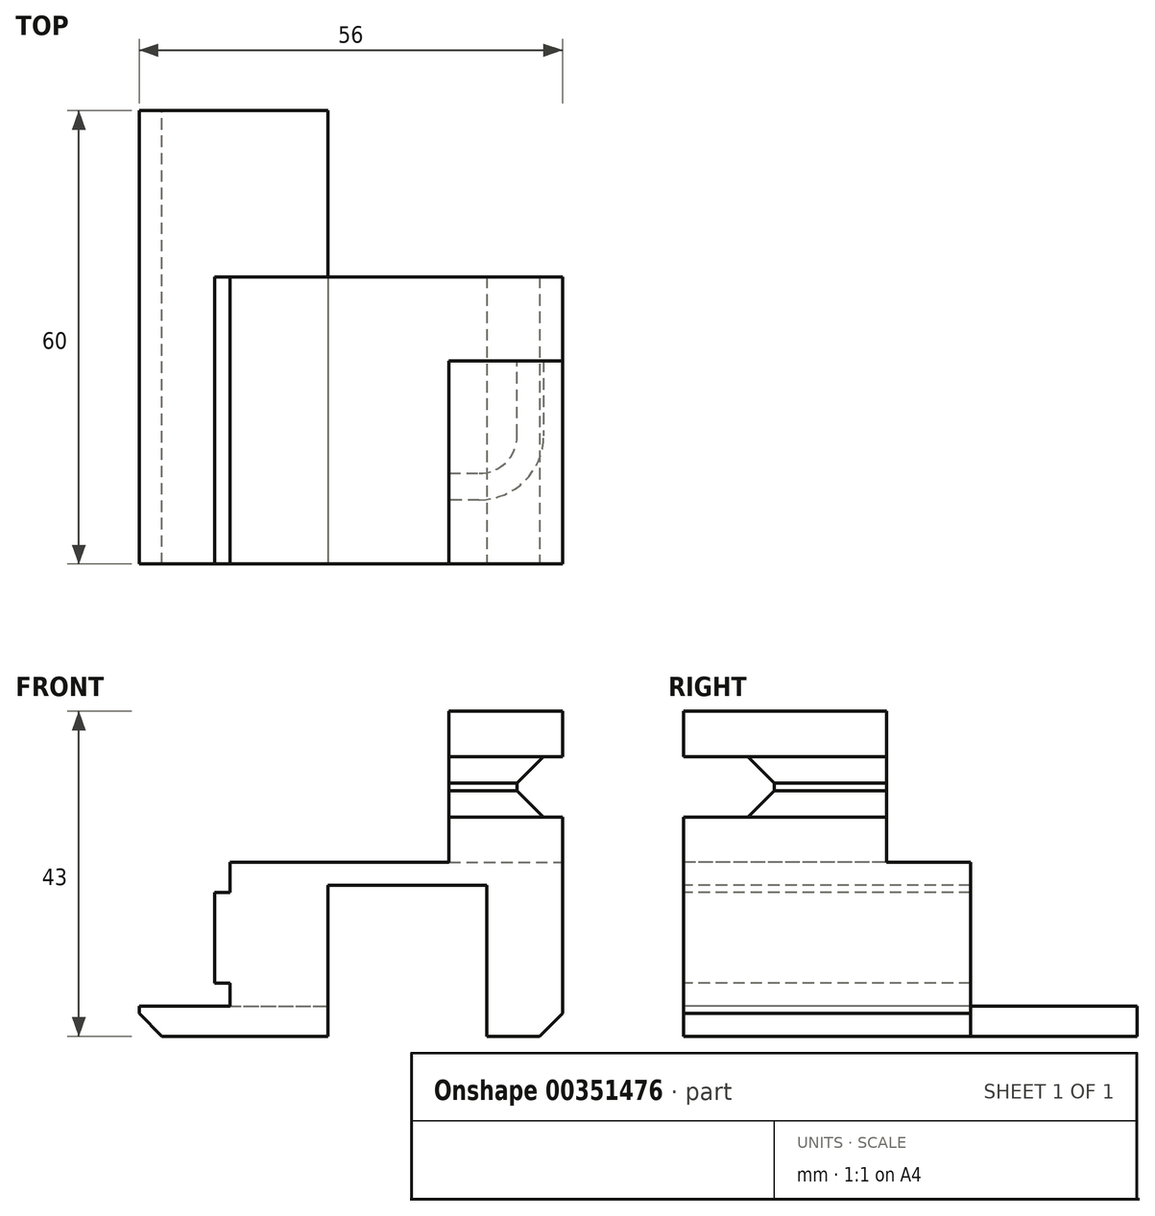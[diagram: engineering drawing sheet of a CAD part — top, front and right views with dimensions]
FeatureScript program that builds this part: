
annotation { "Feature Type Name" : "Feature", "Feature Type Description" : "" }
export const myFeature = defineFeature(function(context is Context, id is Id, definition is map)
    precondition{}
    {
        {
            var Q0;
            Q0=qCreatedBy(makeId("Front.planeOp"),FACE);
            var sketch = newSketch(context, id + "F0", { "sketchPlane" : qUnion([Q0])});
            skLineSegment(sketch, "E0", {"start": v(0, 0) * mm, "end": v(25, 0) * mm});
            skLineSegment(sketch, "E1", {"start": v(25, 0) * mm, "end": v(25, 20) * mm});
            skLineSegment(sketch, "E2", {"start": v(25, 20) * mm, "end": v(46, 20) * mm});
            skLineSegment(sketch, "E3", {"start": v(46, 20) * mm, "end": v(46, 0) * mm});
            skLineSegment(sketch, "E4", {"start": v(46, 0) * mm, "end": v(56, 0) * mm});
            skLineSegment(sketch, "E5", {"start": v(56, 0) * mm, "end": v(56, 43) * mm});
            skLineSegment(sketch, "E6", {"start": v(56, 43) * mm, "end": v(41, 43) * mm});
            skLineSegment(sketch, "E7", {"start": v(41, 43) * mm, "end": v(41, 23) * mm});
            skLineSegment(sketch, "E8", {"start": v(41, 23) * mm, "end": v(0, 23) * mm});
            skLineSegment(sketch, "E9", {"start": v(0, 23) * mm, "end": v(0, 0) * mm});
            skLineSegment(sketch, "E10", {"start": v(0, 4) * mm, "end": v(10, 4) * mm});
            skLineSegment(sketch, "E11", {"start": v(10, 4) * mm, "end": v(10, 23) * mm});
            skSolve(sketch);
        }
        {
            var Q0;
            {var subQ4=sQuery(id+"F0.wireOp",EDGE,"E0");Q0=makeQuery(id+"F0.imprint","IMPRINT",FACE,{"disambiguationData":[TD([[makeQuery(id+"F0.imprint","IMPRINT",EDGE,{"derivedFrom":subQ4}),1.0]])]});}
            extrude(context, id + "F1", {"entities" : qUnion([Q0]), "oppositeDirection" : true, "depth" : 60 * mm});
        }
        {
            var Q0;
            Q0=makeQuery(id+"F1.opExtrude","CAP_FACE",FACE,{"disambiguationData":[OSD([sQuery(id+"F0.wireOp",EDGE,"E0"),sQuery(id+"F0.wireOp",EDGE,"E1"),sQuery(id+"F0.wireOp",EDGE,"E2"),sQuery(id+"F0.wireOp",EDGE,"E3"),sQuery(id+"F0.wireOp",EDGE,"E4"),sQuery(id+"F0.wireOp",EDGE,"E5"),sQuery(id+"F0.wireOp",EDGE,"E6"),sQuery(id+"F0.wireOp",EDGE,"E7"),sQuery(id+"F0.wireOp",EDGE,"E8"),sQuery(id+"F0.wireOp",EDGE,"E9")])],"isStart":false});
            var sketch = newSketch(context, id + "F2", { "sketchPlane" : qUnion([Q0])});
            skLineSegment(sketch, "E12.0", {"start": v(0, 4) * mm, "end": v(-100, 4) * mm});
            skLineSegment(sketch, "E13", {"start": v(0, 4) * mm, "end": v(0, 104) * mm});
            skLineSegment(sketch, "E14", {"start": v(0, 104) * mm, "end": v(-100, 104) * mm});
            skLineSegment(sketch, "E15", {"start": v(-100, 104) * mm, "end": v(-100, 4) * mm});
            skSolve(sketch);
        }
        {
            var Q0;
            Q0 = qSketchRegion(id + "F2", true);
            extrude(context, id + "F3", {"entities" : qUnion([Q0]), "operationType" : NewBodyOperationType.REMOVE, "oppositeDirection" : true, "depth" : 22 * mm});
        }
        {
            var Q0;
            Q0=makeQuery(id+"F3.boolean.opBoolean","COPY",FACE,{"derivedFrom":makeQuery(id+"F3.opExtrude","CAP_FACE",FACE,{"disambiguationData":[OSD([sQuery(id+"F2.wireOp",EDGE,"E12.0"),sQuery(id+"F2.wireOp",EDGE,"E13"),sQuery(id+"F2.wireOp",EDGE,"E14"),sQuery(id+"F2.wireOp",EDGE,"E15")])],"isStart":false})});
            var sketch = newSketch(context, id + "F4", { "sketchPlane" : qUnion([Q0])});
            skLineSegment(sketch, "E16.0.1", {"start": v(-41, 23) * mm, "end": v(-10, 23) * mm});
            skLineSegment(sketch, "E16.0.3", {"start": v(-10, 23) * mm, "end": v(-110, 23) * mm});
            skLineSegment(sketch, "E17", {"start": v(-10, 23) * mm, "end": v(-10, 123) * mm});
            skLineSegment(sketch, "E18", {"start": v(-10, 123) * mm, "end": v(-110, 123) * mm});
            skLineSegment(sketch, "E19", {"start": v(-110, 123) * mm, "end": v(-110, 23) * mm});
            skPoint(sketch, "E20.orphan", {"position": v(-41, 23) * mm});
            skSolve(sketch);
        }
        {
            var Q0;
            Q0 = qSketchRegion(id + "F4", true);
            extrude(context, id + "F5", {"entities" : qUnion([Q0]), "operationType" : NewBodyOperationType.REMOVE, "oppositeDirection" : true, "depth" : 11.1 * mm});
        }
        {
            var Q0;
            Q0=qCreatedBy(makeId("Front.planeOp"),FACE);
            var sketch = newSketch(context, id + "F6", { "sketchPlane" : qUnion([Q0])});
            skLineSegment(sketch, "E21.0", {"start": v(41, 37) * mm, "end": v(41, 29) * mm});
            skLineSegment(sketch, "E22.0", {"start": v(56, 29) * mm, "end": v(56, 37) * mm});
            skLineSegment(sketch, "E23", {"start": v(41, 29) * mm, "end": v(56, 29) * mm});
            skLineSegment(sketch, "E24", {"start": v(41, 37) * mm, "end": v(56, 37) * mm});
            skSolve(sketch);
        }
        {
            var Q0;
            Q0 = qSketchRegion(id + "F6", true);
            extrude(context, id + "F7", {"entities" : qUnion([Q0]), "operationType" : NewBodyOperationType.REMOVE, "oppositeDirection" : true, "depth" : 12 * mm});
        }
        {
            var Q0;
            Q0=qCreatedBy(makeId("Front.planeOp"),FACE);
            var sketch = newSketch(context, id + "F8", { "sketchPlane" : qUnion([Q0])});
            skLineSegment(sketch, "E25.0", {"start": v(50, 37) * mm, "end": v(56, 37) * mm});
            skLineSegment(sketch, "E26.0", {"start": v(50, 29) * mm, "end": v(56, 29) * mm});
            skLineSegment(sketch, "E27.0", {"start": v(56, 29) * mm, "end": v(56, 37) * mm});
            skLineSegment(sketch, "E28", {"start": v(50, 37) * mm, "end": v(50, 29) * mm});
            skSolve(sketch);
        }
        {
            var Q0;
            Q0 = qSketchRegion(id + "F8", true);
            extrude(context, id + "F9", {"entities" : qUnion([Q0]), "operationType" : NewBodyOperationType.REMOVE, "endBound" : BoundingType.THROUGH_ALL, "oppositeDirection" : true, "depth" : 25 * mm});
        }
        {
            var Q0;
            Q0=qCreatedBy(makeId("Front.planeOp"),FACE);
            var sketch = newSketch(context, id + "F10", { "sketchPlane" : qUnion([Q0])});
            skLineSegment(sketch, "E29.0", {"start": v(10, 4) * mm, "end": v(12, 4) * mm});
            skLineSegment(sketch, "E30.0", {"start": v(10, 4) * mm, "end": v(10, 7) * mm});
            skLineSegment(sketch, "E31.0", {"start": v(12, 23) * mm, "end": v(10, 23) * mm});
            skLineSegment(sketch, "E32", {"start": v(12, 23) * mm, "end": v(12, 19) * mm});
            skLineSegment(sketch, "E33", {"start": v(12, 19) * mm, "end": v(10, 19) * mm});
            skLineSegment(sketch, "E34", {"start": v(10, 7) * mm, "end": v(12, 7) * mm});
            skLineSegment(sketch, "E35", {"start": v(12, 7) * mm, "end": v(12, 4) * mm});
            skLineSegment(sketch, "E36.trimOffspring", {"start": v(10, 19) * mm, "end": v(10, 23) * mm});
            skSolve(sketch);
        }
        {
            var Q0;
            Q0 = qSketchRegion(id + "F10", true);
            extrude(context, id + "F11", {"entities" : qUnion([Q0]), "operationType" : NewBodyOperationType.REMOVE, "endBound" : BoundingType.THROUGH_ALL, "oppositeDirection" : true, "depth" : 25 * mm});
        }
        {
            var Q0;
            {var subQ0=sQuery(id+"F0.wireOp",EDGE,"E10");var subQ1=sQuery(id+"F0.wireOp",EDGE,"E9");var subQ2=sQuery(id+"F0.wireOp",EDGE,"E0");var subQ3=sQuery(id+"F0.wireOp",EDGE,"E1");Q0=makeQuery(id+"F3.boolean.opBoolean","SPLIT",FACE,{"disambiguationData":[TD([makeQuery(id+"F1.opExtrude","SWEPT_FACE",FACE,{"disambiguationData":[OSD([subQ2])]})])],"derivedFrom":makeQuery(id+"F1.opExtrude","CAP_FACE",FACE,{"disambiguationData":[OSD([subQ2,subQ3,sQuery(id+"F0.wireOp",EDGE,"E2"),sQuery(id+"F0.wireOp",EDGE,"E3"),sQuery(id+"F0.wireOp",EDGE,"E4"),sQuery(id+"F0.wireOp",EDGE,"E5"),sQuery(id+"F0.wireOp",EDGE,"E6"),sQuery(id+"F0.wireOp",EDGE,"E7"),sQuery(id+"F0.wireOp",EDGE,"E8"),subQ1,subQ0,sQuery(id+"F0.wireOp",EDGE,"E11")])],"isStart":false})});}
            var sketch = newSketch(context, id + "F12", { "sketchPlane" : qUnion([Q0])});
            skPoint(sketch, "E37.firstSnap0", {"position": v(-12.5, 0) * mm});
            skLineSegment(sketch, "E37.bottom", {"start": v(-60, 0) * mm, "end": v(-30, 0) * mm});
            skLineSegment(sketch, "E37.top", {"start": v(-60, 15) * mm, "end": v(-30, 15) * mm});
            skLineSegment(sketch, "E37.left", {"start": v(-60, 0) * mm, "end": v(-60, 15) * mm});
            skLineSegment(sketch, "E37.right", {"start": v(-30, 0) * mm, "end": v(-30, 15) * mm});
            skSolve(sketch);
        }
        {
            var Q0;
            Q0 = qSketchRegion(id + "F12", true);
            var Q1;
            Q1=makeQuery(id+"F3.boolean.opBoolean","COPY",FACE,{"derivedFrom":makeQuery(id+"F3.opExtrude","CAP_FACE",FACE,{"disambiguationData":[OSD([sQuery(id+"F2.wireOp",EDGE,"E12.0"),sQuery(id+"F2.wireOp",EDGE,"E13"),sQuery(id+"F2.wireOp",EDGE,"E14"),sQuery(id+"F2.wireOp",EDGE,"E15")])],"isStart":false})});
            extrude(context, id + "F13", {"entities" : qUnion([Q0]), "operationType" : NewBodyOperationType.REMOVE, "endBound" : BoundingType.UP_TO_SURFACE, "oppositeDirection" : true, "endBoundEntityFace" : qUnion([Q1]), "depth" : 25 * mm});
        }
        {
            var Q0;
            Q0=makeQuery(id+"F1.opExtrude","SWEPT_EDGE",EDGE,{"disambiguationData":[OSD([sQuery(id+"F0.wireOp",EDGE,"E4"),sQuery(id+"F0.wireOp",EDGE,"E5")])]});
            var Q1;
            Q1=makeQuery(id+"F1.opExtrude","SWEPT_EDGE",EDGE,{"disambiguationData":[OSD([sQuery(id+"F0.wireOp",EDGE,"E0"),sQuery(id+"F0.wireOp",EDGE,"E9")])]});
            chamfer(context, id + "F14", {"entities" : qUnion([Q0, Q1]), "width" : 3 * mm, "tangentPropagation" : true});
        }
        {
            var Q0;
            Q0=makeQuery(id+"F9.boolean.opBoolean","INTERSECT",EDGE,{"derivedFrom":[makeQuery(id+"F7.boolean.opBoolean","COPY",FACE,{"derivedFrom":makeQuery(id+"F7.opExtrude","CAP_FACE",FACE,{"disambiguationData":[OSD([sQuery(id+"F6.wireOp",EDGE,"E21.0"),sQuery(id+"F6.wireOp",EDGE,"E22.0"),sQuery(id+"F6.wireOp",EDGE,"E23"),sQuery(id+"F6.wireOp",EDGE,"E24")])],"isStart":false})}),makeQuery(id+"F9.opExtrude","SWEPT_FACE",FACE,{"disambiguationData":[OSD([sQuery(id+"F8.wireOp",EDGE,"E28")])]})]});
            fillet(context, id + "F15", {"entities" : qUnion([Q0]), "radius" : 5 * mm, "tangentPropagation" : true, "allowEdgeOverflow" : false});
        }
        {
            var Q0;
            Q0=makeQuery(id+"F7.boolean.opBoolean","COPY",EDGE,{"derivedFrom":makeQuery(id+"F7.opExtrude","CAP_EDGE",EDGE,{"disambiguationData":[OSD([sQuery(id+"F6.wireOp",EDGE,"E24")])],"isStart":false})});
            var Q1;
            Q1=makeQuery(id+"F7.boolean.opBoolean","COPY",EDGE,{"derivedFrom":makeQuery(id+"F7.opExtrude","CAP_EDGE",EDGE,{"disambiguationData":[OSD([sQuery(id+"F6.wireOp",EDGE,"E23")])],"isStart":false})});
            chamfer(context, id + "F16", {"entities" : qUnion([Q0, Q1]), "width" : 3.5 * mm, "tangentPropagation" : true});
        }
    });
